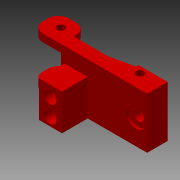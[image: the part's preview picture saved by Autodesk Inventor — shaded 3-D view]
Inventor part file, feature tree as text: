
AUTODESK INVENTOR PART (.ipt)
format: ipt  version: 2013 (Build 170138000, 138)  size: 208,896 bytes
history: native  units: mm
features: extrude x7, sketch x7, projected_geometry x1
ambient origin geometry x8: Origin, YZ Plane, XZ Plane, XY Plane, X Axis, Y Axis, Z Axis, Center Point
bodies: Solid1 (feature_tree)
feature tree (15):
  extrude  "Extrusion1"  Depth=14.0mm TaperAngle=0.0deg
  extrude  "Extrusion2"  Depth=5.0mm
  extrude  "Extrusion3"  Depth=4.098299mm
  extrude  "Extrusion4"  Depth=3.368868mm
  extrude  "Extrusion5"  Depth=6.631132mm
  extrude  "Extrusion6"  Depth=10.0mm TaperAngle=0.0deg
  extrude  "Extrusion7"  Depth=10.0mm TaperAngle=0.0deg
  sketch  "Sketch1"  dims[d0=3.0mm d1=0.0mm d2=14.0mm d3=0.0mm]
  sketch  "Sketch2"  dims[d4=3.0mm d5=0.0mm d6=5.0mm]
  sketch  "Sketch4"  dims[d8=5.0mm d9=4.098299mm]
  projected_geometry  "Projected Loop1"
  sketch  "Sketch5"  dims[d10=4.698465mm d11=3.368868mm]
  sketch  "Sketch6"  dims[d12=4.344234mm d13=6.631132mm]
  sketch  "Sketch7"  dims[d14=1.4mm d15=10.0mm d16=0.0mm]
  sketch  "Sketch8"  dims[d17=2.0mm d19=10.0mm d20=0.0mm d21=4.3mm d22=10.0mm d23=8.0mm d24=1.0mm d25=0.0mm d26=4.0mm d28=11.0mm d29=0.0mm]
